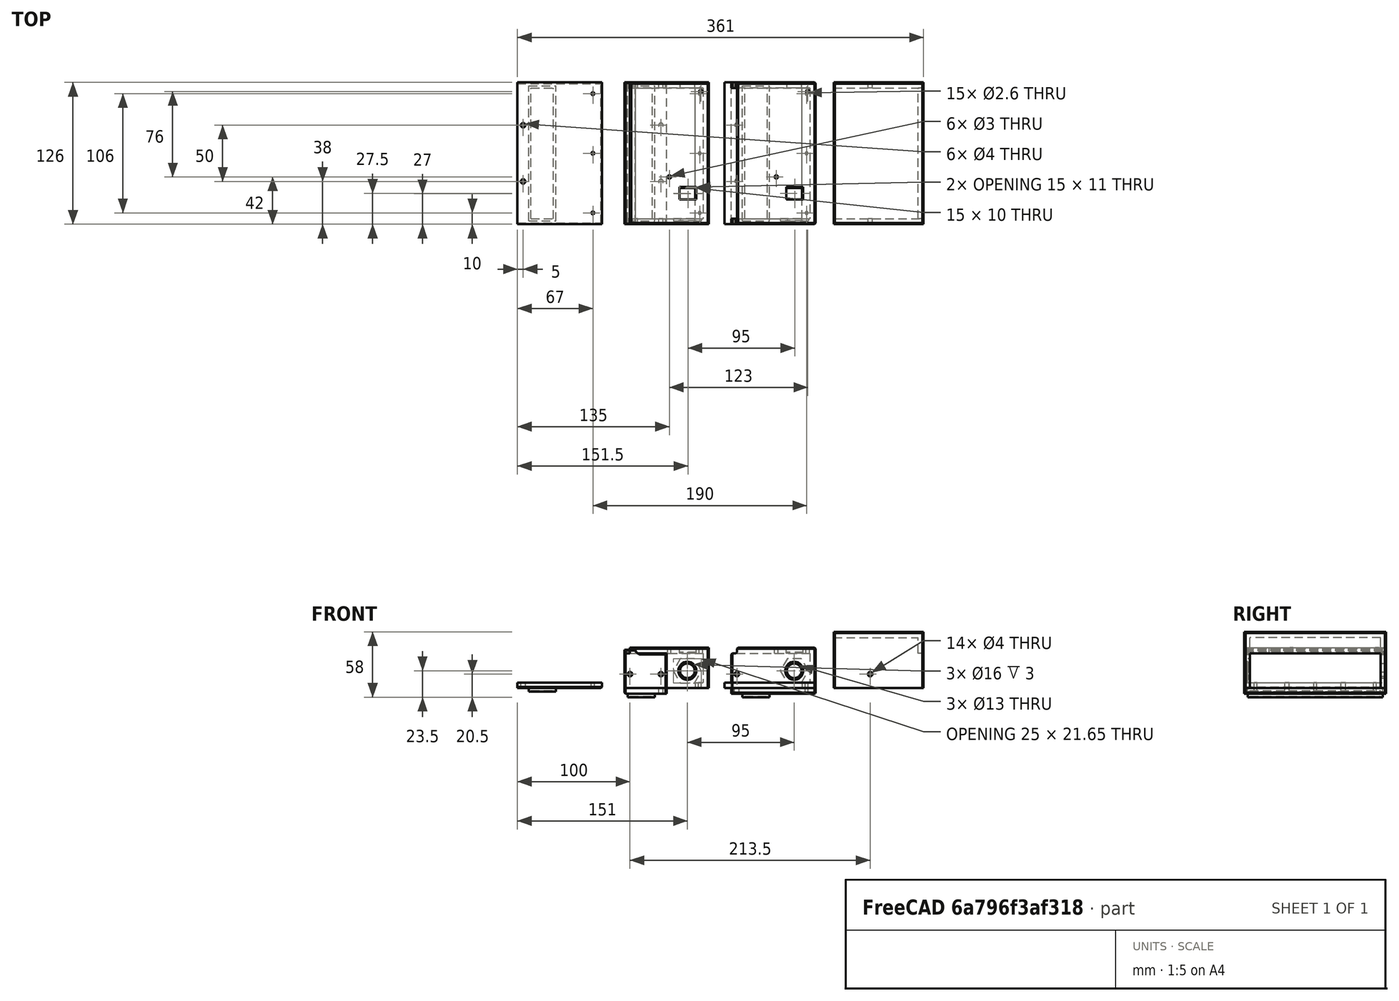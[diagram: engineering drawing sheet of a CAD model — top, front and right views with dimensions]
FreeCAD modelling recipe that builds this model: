
FCSTD DOCUMENT  (FreeCAD 0.18R14555 (Git shallow))
Label: meanwell-psu-sonoff-mounter
License: All rights reserved
LicenseURL: http://en.wikipedia.org/wiki/All_rights_reserved
objects: Part::Box×21, Part::Cut×15, Part::Cylinder×14, Part::Feature×12, Part::Chamfer×11, Part::MultiFuse×10
note: 83 computed .brp shape members not serialized (recipe doc carries the construction recipe); baked Part::Feature solids carry a one-line shape summary decoded from their .brp

FEATURE [Part::Box] Box  label="Cube"
  AttacherType = Attacher::AttachEngine3D
  Height = 5
  Length = 75
  Width = 126
FEATURE [Part::Box] Box001  label="Cube001"
  AttacherType = Attacher::AttachEngine3D
  Height = 41
  Length = 75
  Width = 5
FEATURE [Part::Box] Box002  label="Cube002"
  AttacherType = Attacher::AttachEngine3D
  Height = 41
  Length = 75
  Placement = pos=(0,121,0) rot=(0,0,1;0rad)
  Width = 5
FEATURE [Part::Box] Box003  label="Cube003"
  AttacherType = Attacher::AttachEngine3D
  Height = 5
  Length = 75
  Placement = pos=(0,0,36) rot=(0,0,1;0rad)
  Width = 126
FEATURE [Part::Box] Box004  label="Cube004"
  AttacherType = Attacher::AttachEngine3D
  Height = 41
  Length = 5
  Placement = pos=(70,0,0) rot=(0,0,1;0rad)
  Width = 126
FEATURE [Part::Feature] Body001
  Placement = pos=(37,8,-2.5) rot=(0,0,1;0rad)
  shape: bbox 25 x 5 x 21.65 mm, 8 faces (baked)
FEATURE [Part::Cylinder] Cylinder
  Angle = 360
  AttacherType = Attacher::AttachEngine3D
  Height = 10
  Placement = pos=(56,9,20.5) rot=(1,0,0;1.5708rad)
  Radius = 8
FEATURE [Part::Cut] Cut
  Base = -> Box001
  Tool = -> Body001
FEATURE [Part::Cut] Cut001
  Base = -> Cut
  Tool = -> Cylinder
FEATURE [Part::MultiFuse] Fusion
  Shapes = -> [Cut001,Box004,Box003,Box002,Box]
FEATURE [Part::Cylinder] Cylinder001
  Angle = 360
  AttacherType = Attacher::AttachEngine3D
  Height = 10
  Placement = pos=(56,118,20.5) rot=(-1,0,0;1.5708rad)
  Radius = 6.5
FEATURE [Part::Cylinder] Cylinder002
  Angle = 360
  AttacherType = Attacher::AttachEngine3D
  Height = 5
  Radius = 1.5
FEATURE [Part::Cylinder] Cylinder003
  Angle = 360
  AttacherType = Attacher::AttachEngine3D
  Height = 5
  Placement = pos=(28,76,0) rot=(0,0,1;0rad)
  Radius = 1.5
FEATURE [Part::MultiFuse] Fusion001
  Placement = pos=(68,118,36) rot=(0,0,1;3.14159rad)
  Shapes = -> [Cylinder003,Cylinder002]
FEATURE [Part::Box] Box005  label="Cube005"
  AttacherType = Attacher::AttachEngine3D
  Height = 10
  Length = 15
  Placement = pos=(49,22,34) rot=(0,0,1;0rad)
  Width = 10
FEATURE [Part::Box] Box006  label="Cube006"
  AttacherType = Attacher::AttachEngine3D
  Height = 5
  Length = 75
  Width = 126
FEATURE [Part::Box] Box007  label="Cube007"
  AttacherType = Attacher::AttachEngine3D
  Height = 5
  Length = 12
  Placement = pos=(63,0,5) rot=(0,0,1;0rad)
  Width = 126
FEATURE [Part::Cut] Cut002
  Base = -> Fusion
  Tool = -> Box006
FEATURE [Part::Cut] Cut003
  Base = -> Cut002
  Tool = -> Cylinder001
FEATURE [Part::Cut] Cut004
  Base = -> Cut003
  Tool = -> Fusion001
FEATURE [Part::Cut] Cut005
  Base = -> Cut004
  Tool = -> Box005
FEATURE [Part::MultiFuse] Fusion002
  Shapes = -> [Cut005,Box007]
FEATURE [Part::Box] Box008  label="Cube008"
  AttacherType = Attacher::AttachEngine3D
  Height = 5
  Length = 5
  Placement = pos=(0,0,36) rot=(0,0,1;0rad)
  Width = 126
FEATURE [Part::Cut] Cut006
  Base = -> Fusion002
  Tool = -> Box008
FEATURE [Part::Cylinder] Cylinder004
  Angle = 360
  AttacherType = Attacher::AttachEngine3D
  Height = 126
  Placement = pos=(5,4e-15,17.5) rot=(-1,0,0;1.5708rad)
  Radius = 2
FEATURE [Part::Cut] Cut007
  Base = -> Cut006
  Tool = -> Cylinder004
FEATURE [Part::Cylinder] Cylinder005
  Angle = 360
  AttacherType = Attacher::AttachEngine3D
  Height = 10
  Placement = pos=(67,10,5) rot=(0,0,1;0rad)
  Radius = 1.3
FEATURE [Part::Cylinder] Cylinder006
  Angle = 360
  AttacherType = Attacher::AttachEngine3D
  Height = 10
  Placement = pos=(67,116,5) rot=(0,0,1;0rad)
  Radius = 1.3
FEATURE [Part::Cylinder] Cylinder007
  Angle = 360
  AttacherType = Attacher::AttachEngine3D
  Height = 10
  Placement = pos=(67,63,5) rot=(0,0,1;0rad)
  Radius = 1.3
FEATURE [Part::MultiFuse] Fusion003
  Shapes = -> [Cylinder007,Cylinder006,Cylinder005]
FEATURE [Part::Cut] Cut008
  Base = -> Cut007
  Tool = -> Fusion003
FEATURE [Part::Feature] Cut008001  label="Cut009"
  shape: bbox 75 x 126 x 36 mm, 36 faces (baked)
FEATURE [Part::Chamfer] Chamfer
  Base = -> Cut008001
  Edges = 7 edges r=1: [Edge52,Edge73,Edge87,Edge90,Edge91,Edge96,Edge97]
FEATURE [Part::Chamfer] Chamfer001
  Base = -> Chamfer
  Edges = 6 edges r=1: [Edge29,Edge31,Edge67,Edge73,Edge77,Edge81]
FEATURE [Part::Feature] Chamfer001_solid  label="Chamfer001 (Solid)"
  Placement = pos=(95,0,0) rot=(0,0,1;0rad)
  shape: bbox 75 x 126 x 36 mm, 50 faces (baked)
FEATURE [Part::Box] Box009  label="Cube009"
  AttacherType = Attacher::AttachEngine3D
  Height = 5
  Length = 75
  Placement = pos=(0,0,5) rot=(0,0,1;0rad)
  Width = 126
FEATURE [Part::Feature] Fusion003001  label="Fusion004"
  shape: bbox 2.6 x 108.6 x 10 mm, 9 faces, 3 solids (baked)
FEATURE [Part::Cut] Cut008002
  Base = -> Box009
  Placement = pos=(-95,0,0) rot=(0,0,1;0rad)
  Tool = -> Fusion003001
FEATURE [Part::Cylinder] Cylinder008
  Angle = 360
  AttacherType = Attacher::AttachEngine3D
  Height = 10
  Placement = pos=(-90,38,0) rot=(0,0,1;0rad)
  Radius = 2
FEATURE [Part::Cylinder] Cylinder009
  Angle = 360
  AttacherType = Attacher::AttachEngine3D
  Height = 10
  Placement = pos=(-90,88,0) rot=(0,0,1;0rad)
  Radius = 2
FEATURE [Part::MultiFuse] Fusion003002
  Shapes = -> [Cylinder009,Cylinder008]
FEATURE [Part::Cut] Cut008003
  Base = -> Cut008002
  Tool = -> Fusion003002
FEATURE [Part::Box] Box010  label="Cube010"
  AttacherType = Attacher::AttachEngine3D
  Height = 1
  Length = 20
  Placement = pos=(-83,5,2) rot=(0,0,1;0rad)
  Width = 116
FEATURE [Part::Box] Box011  label="Cube011"
  AttacherType = Attacher::AttachEngine3D
  Height = 3
  Length = 24
  Placement = pos=(-85,3,2) rot=(0,0,1;0rad)
  Width = 120
FEATURE [Part::Cut] Cut008004
  Base = -> Box011
  Tool = -> Box010
FEATURE [Part::Box] Box012  label="Cube012"
  AttacherType = Attacher::AttachEngine3D
  Height = 5
  Length = 80
  Placement = pos=(89,0,5) rot=(0,0,1;0rad)
  Width = 126
FEATURE [Part::Box] Box013  label="Cube013"
  AttacherType = Attacher::AttachEngine3D
  Height = 5
  Length = 80
  Placement = pos=(186,0,50) rot=(0,0,1;0rad)
  Width = 126
FEATURE [Part::Feature] Cut008004001  label="Cut008005"
  Placement = pos=(88,0,-5) rot=(0,0,1;0rad)
  shape: bbox 24 x 120 x 3 mm, 11 faces (baked)
FEATURE [Part::Box] Box014  label="Cube014"
  AttacherType = Attacher::AttachEngine3D
  Height = 50
  Length = 80
  Placement = pos=(186,0,5) rot=(0,0,1;0rad)
  Width = 5
FEATURE [Part::Box] Box015  label="Cube015"
  AttacherType = Attacher::AttachEngine3D
  Height = 50
  Length = 80
  Placement = pos=(186,121,5) rot=(0,0,1;0rad)
  Width = 5
FEATURE [Part::Box] Box016  label="Cube016"
  AttacherType = Attacher::AttachEngine3D
  Height = 19
  Length = 5
  Placement = pos=(261,0,36) rot=(0,0,1;0rad)
  Width = 126
FEATURE [Part::Cylinder] Cylinder012
  Angle = 360
  AttacherType = Attacher::AttachEngine3D
  Height = 130
  Placement = pos=(218.5,4e-15,17.5) rot=(-1,0,0;1.5708rad)
  Radius = 2
FEATURE [Part::MultiFuse] Fusion003003
  Shapes = -> [Cut008003,Cut008004]
FEATURE [Part::MultiFuse] Fusion003006
  Shapes = -> [Box016,Box015,Box014,Box013]
FEATURE [Part::Cut] Cut008004003
  Base = -> Fusion003006
  Tool = -> Cylinder012
FEATURE [Part::Chamfer] Chamfer002
  Base = -> Fusion003003
  Edges = 2 edges r=1: [Edge5,Edge15]
FEATURE [Part::Chamfer] Chamfer004
  Base = -> Chamfer002
  Edges = 1 edges r=1: [Edge20]
FEATURE [Part::Feature] Cut008004003001  label="Cut008004004"
  shape: bbox 80 x 126 x 50 mm, 14 faces (baked)
FEATURE [Part::Chamfer] Chamfer006
  Base = -> Cut008004003001
  Edges = 8 edges r=1: [Edge29,Edge30,Edge31,Edge32,Edge33,Edge34,Edge35,Edge36]
FEATURE [Part::Feature] Chamfer004_solid  label="Chamfer004 (Solid)"
  Placement = pos=(190,0,-5) rot=(0,0,1;0rad)
  shape: bbox 75 x 126 x 8 mm, 24 faces (baked)
FEATURE [Part::Box] Box017  label="Cube017"
  AttacherType = Attacher::AttachEngine3D
  Height = 5
  Length = 37.5
  Width = 126
FEATURE [Part::Cylinder] Cylinder013
  Angle = 360
  AttacherType = Attacher::AttachEngine3D
  Height = 10
  Placement = pos=(32.5,38,0) rot=(0,0,1;0rad)
  Radius = 2
FEATURE [Part::Cylinder] Cylinder014
  Angle = 360
  AttacherType = Attacher::AttachEngine3D
  Height = 10
  Placement = pos=(32.5,88,0) rot=(0,0,1;0rad)
  Radius = 2
FEATURE [Part::MultiFuse] Fusion003007
  Shapes = -> [Cylinder013,Cylinder014]
FEATURE [Part::Cut] Cut008004003002
  Base = -> Box017
  Tool = -> Fusion003007
FEATURE [Part::MultiFuse] Fusion003008
  Shapes = -> [Cut008004003002,Cut008004001]
FEATURE [Part::Box] Box018  label="Cube018"
  AttacherType = Attacher::AttachEngine3D
  Height = 31
  Length = 37.5
  Placement = pos=(0,0,5) rot=(0,0,1;0rad)
  Width = 5
FEATURE [Part::Box] Box019  label="Cube019"
  AttacherType = Attacher::AttachEngine3D
  Height = 31
  Length = 37.5
  Placement = pos=(0,121,5) rot=(0,0,1;0rad)
  Width = 5
FEATURE [Part::Box] Box020  label="Cube020"
  AttacherType = Attacher::AttachEngine3D
  Height = 3
  Length = 10
  Placement = pos=(0,0,36) rot=(0,0,1;0rad)
  Width = 126
FEATURE [Part::Cylinder] Cylinder015
  Angle = 360
  AttacherType = Attacher::AttachEngine3D
  Height = 126
  Placement = pos=(32.5,4e-15,17.5) rot=(-1,0,0;1.5708rad)
  Radius = 2
FEATURE [Part::MultiFuse] Fusion003009
  Shapes = -> [Box018,Box020,Box019]
FEATURE [Part::Chamfer] Chamfer007
  Base = -> Fusion003009
  Edges = 2 edges r=2: [Edge22,Edge32]
FEATURE [Part::Cut] Cut008004003003
  Base = -> Chamfer007
  Tool = -> Cylinder015
FEATURE [Part::Feature] Cut008004003003001  label="Cut008004003004"
  shape: bbox 37.5 x 126 x 34 mm, 18 faces (baked)
FEATURE [Part::Chamfer] Chamfer008
  Base = -> Cut008004003003001
  Edges = 9 edges r=1: [Edge3,Edge4,Edge5,Edge26,Edge39,Edge40,Edge41,Edge47,Edge48]
FEATURE [Part::Chamfer] Chamfer009
  Base = -> Chamfer008
  Edges = 3 edges r=0.5: [Edge24,Edge43,Edge46]
FEATURE [Part::Feature] Chamfer009_solid  label="top-1"
  shape: bbox 37.5 x 126 x 34 mm, 32 faces (baked)
FEATURE [Part::Chamfer] Chamfer010
  Base = -> Fusion003008
  Edges = 5 edges r=1: [Edge1,Edge3,Edge4,Edge6,Edge13]
FEATURE [Part::Feature] Chamfer010_solid  label="bottom-1"
  shape: bbox 37.5 x 126 x 8 mm, 23 faces (baked)
FEATURE [Part::Chamfer] Chamfer011  label="bottom-2"
  Base = -> Chamfer004_solid
  Edges = 4 edges r=1: [Edge19,Edge21,Edge23,Edge44]
FEATURE [Part::Chamfer] Chamfer012  label="top2"
  Base = -> Chamfer001_solid
  Edges = 1 edges r=1: [Edge40]
FEATURE [Part::Feature] Chamfer011_solid  label="bottom-2 (Solid)"
  shape: bbox 75 x 126 x 8 mm, 28 faces (baked)
FEATURE [Part::Feature] Chamfer012_solid  label="top2 (Solid)"
  shape: bbox 75 x 126 x 36 mm, 51 faces (baked)
